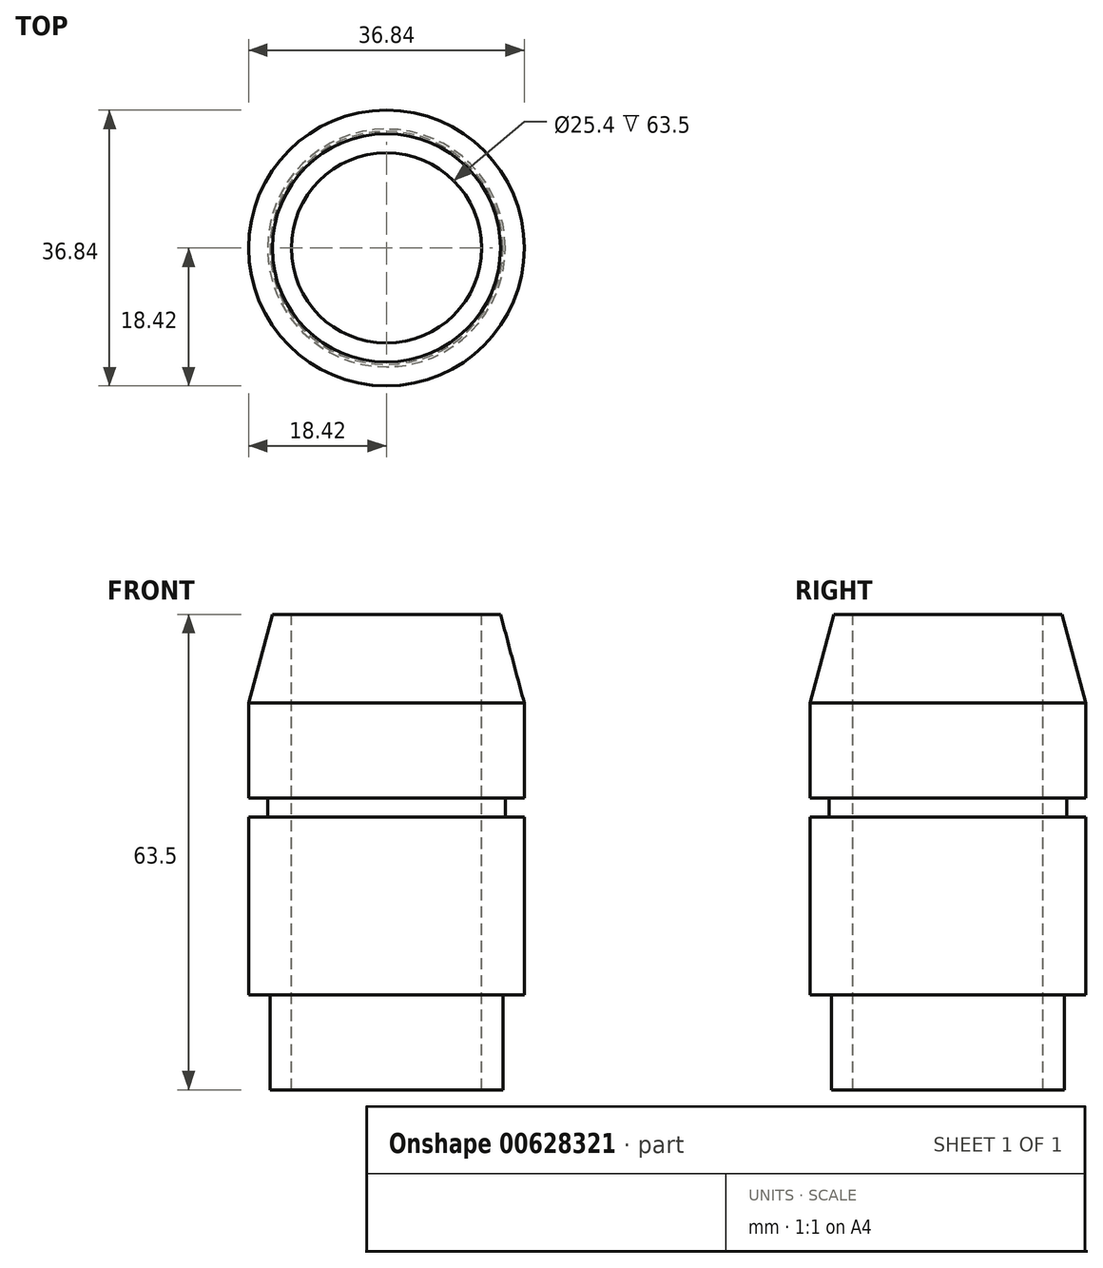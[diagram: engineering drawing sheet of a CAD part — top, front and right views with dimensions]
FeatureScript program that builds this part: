
annotation { "Feature Type Name" : "Feature", "Feature Type Description" : "" }
export const myFeature = defineFeature(function(context is Context, id is Id, definition is map)
    precondition{}
    {
        {
            var Q0;
            Q0=qCreatedBy(makeId("Front.planeOp"),FACE);
            var sketch = newSketch(context, id + "F0", { "sketchPlane" : qUnion([Q0])});
            skLineSegment(sketch, "E0", {"start": v(12.7, 41.79) * mm, "end": v(15.24, 41.79) * mm});
            skLineSegment(sketch, "E1", {"start": v(15.24, 41.79) * mm, "end": v(18.41, 29.94) * mm});
            skLineSegment(sketch, "E2", {"start": v(18.41, 29.94) * mm, "end": v(18.41, 17.24) * mm});
            skLineSegment(sketch, "E3", {"start": v(18.41, 17.24) * mm, "end": v(15.87, 17.24) * mm});
            skLineSegment(sketch, "E4", {"start": v(15.87, 17.24) * mm, "end": v(15.87, 14.7) * mm});
            skLineSegment(sketch, "E5", {"start": v(15.87, 14.7) * mm, "end": v(18.42, 14.7) * mm});
            skLineSegment(sketch, "E6", {"start": v(0, 41.79) * mm, "end": v(0, -21.71) * mm});
            skLineSegment(sketch, "E7", {"start": v(12.7, -21.71) * mm, "end": v(15.56, -21.71) * mm});
            skLineSegment(sketch, "E8", {"start": v(18.42, -9.01) * mm, "end": v(18.42, 14.7) * mm});
            skLineSegment(sketch, "E9", {"start": v(18.42, -9.01) * mm, "end": v(15.56, -9.01) * mm});
            skLineSegment(sketch, "E10", {"start": v(15.56, -21.71) * mm, "end": v(15.56, -9.01) * mm});
            skLineSegment(sketch, "E11", {"start": v(12.7, 41.79) * mm, "end": v(12.7, -21.71) * mm});
            skSolve(sketch);
        }
        {
            var Q0;
            Q0=makeQuery(id+"F0.imprint","IMPRINT",FACE,{"disambiguationData":[TD([[makeQuery(id+"F0.imprint","IMPRINT",EDGE,{"derivedFrom":sQuery(id+"F0.wireOp",EDGE,"E0")}),-1.0]])]});
            var Q1;
            Q1=sQuery(id+"F0.wireOp",EDGE,"E6");
            revolve(context, id + "F1", {"entities" : qUnion([Q0]), "axis" : qUnion([Q1]), "revolveType" : RevolveType.FULL});
        }
    });
